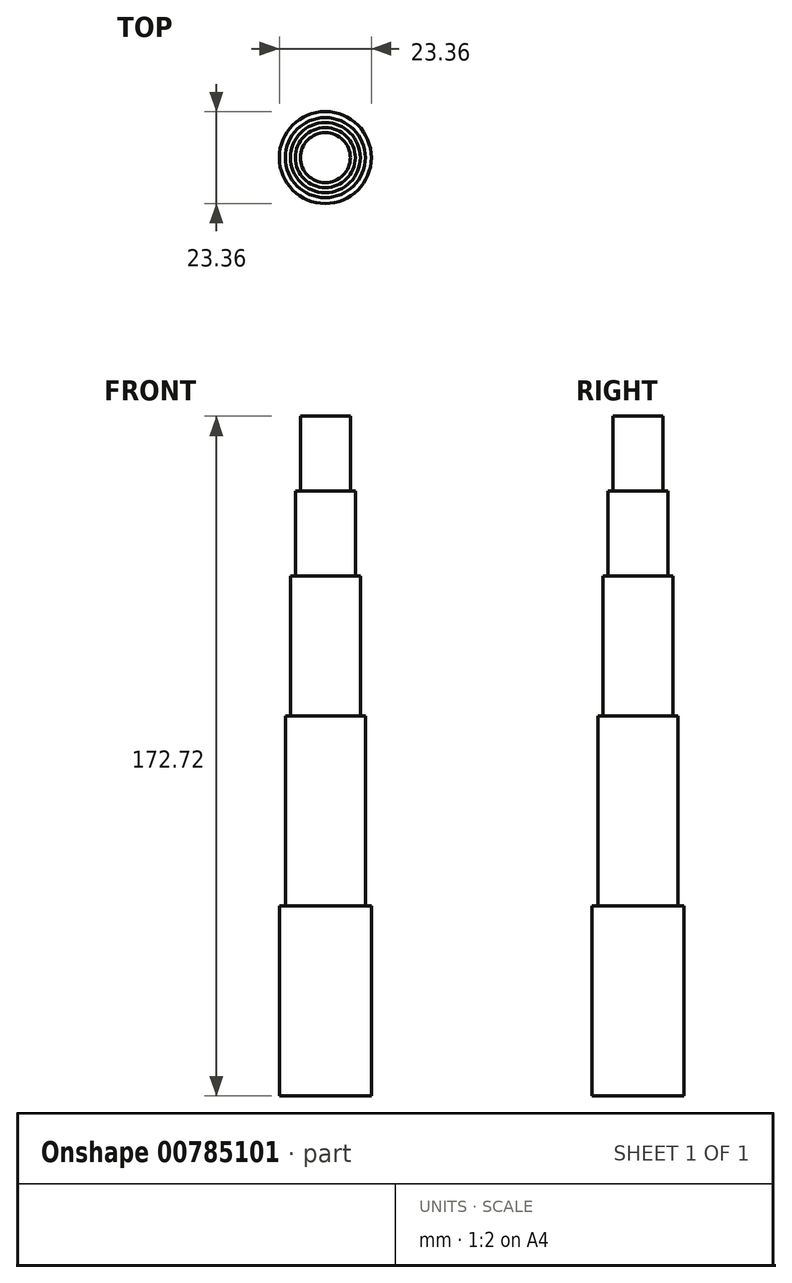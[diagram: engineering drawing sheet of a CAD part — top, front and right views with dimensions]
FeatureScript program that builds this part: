
annotation { "Feature Type Name" : "Feature", "Feature Type Description" : "" }
export const myFeature = defineFeature(function(context is Context, id is Id, definition is map)
    precondition{}
    {
        {
            var Q0;
            Q0=qCreatedBy(makeId("Top.planeOp"),FACE);
            var sketch = newSketch(context, id + "F0", { "sketchPlane" : qUnion([Q0])});
            skCircle(sketch, "E0", {"center": v(0, 0) * mm, "radius": 6.35 * mm});
            skSolve(sketch);
        }
        {
            var Q0;
            Q0 = qSketchRegion(id + "F0", true);
            extrude(context, id + "F1", {"entities" : qUnion([Q0]), "depth" : 19.05 * mm, "offsetDistance" : 25.4 * mm});
        }
        {
            var Q0;
            Q0=qCreatedBy(makeId("Top.planeOp"),FACE);
            var sketch = newSketch(context, id + "F2", { "sketchPlane" : qUnion([Q0])});
            skCircle(sketch, "E1", {"center": v(0, 0) * mm, "radius": 7.62 * mm});
            skSolve(sketch);
        }
        {
            var Q0;
            Q0 = qSketchRegion(id + "F2", true);
            extrude(context, id + "F3", {"entities" : qUnion([Q0]), "operationType" : NewBodyOperationType.ADD, "oppositeDirection" : true, "depth" : 21.59 * mm, "offsetDistance" : 25.4 * mm});
        }
        {
            var Q0;
            Q0=qCreatedBy(makeId("Top.planeOp"),FACE);
            cPlane(context, id + "F4", {"entities" : qUnion([Q0]), "cplaneType" : CPlaneType.OFFSET, "offset" : 21.59 * mm, "oppositeDirection" : true, "width" : 152.4 * mm, "height" : 152.4 * mm});
        }
        {
            var Q0;
            Q0=qCreatedBy(id+"F4.planeOp",FACE);
            var sketch = newSketch(context, id + "F5", { "sketchPlane" : qUnion([Q0])});
            skCircle(sketch, "E2", {"center": v(0, 0) * mm, "radius": 8.9 * mm});
            skSolve(sketch);
        }
        {
            var Q0;
            Q0 = qSketchRegion(id + "F5", true);
            extrude(context, id + "F6", {"entities" : qUnion([Q0]), "operationType" : NewBodyOperationType.ADD, "oppositeDirection" : true, "depth" : 35.56 * mm, "offsetDistance" : 25.4 * mm});
        }
        {
            var Q0;
            Q0=qCreatedBy(id+"F4.planeOp",FACE);
            cPlane(context, id + "F7", {"entities" : qUnion([Q0]), "cplaneType" : CPlaneType.OFFSET, "offset" : 35.56 * mm, "oppositeDirection" : true, "width" : 152.4 * mm, "height" : 152.4 * mm});
        }
        {
            var Q0;
            Q0=qCreatedBy(id+"F7.planeOp",FACE);
            var sketch = newSketch(context, id + "F8", { "sketchPlane" : qUnion([Q0])});
            skCircle(sketch, "E3", {"center": v(0, 0) * mm, "radius": 10.16 * mm});
            skSolve(sketch);
        }
        {
            var Q0;
            Q0 = qSketchRegion(id + "F8", true);
            extrude(context, id + "F9", {"entities" : qUnion([Q0]), "operationType" : NewBodyOperationType.ADD, "oppositeDirection" : true, "depth" : 48.26 * mm, "offsetDistance" : 25.4 * mm});
        }
        {
            var Q0;
            Q0=qCreatedBy(id+"F7.planeOp",FACE);
            cPlane(context, id + "F10", {"entities" : qUnion([Q0]), "cplaneType" : CPlaneType.OFFSET, "offset" : 48.26 * mm, "oppositeDirection" : true, "width" : 152.4 * mm, "height" : 152.4 * mm});
        }
        {
            var Q0;
            Q0=qCreatedBy(id+"F10.planeOp",FACE);
            var sketch = newSketch(context, id + "F11", { "sketchPlane" : qUnion([Q0])});
            skCircle(sketch, "E4", {"center": v(0, 0) * mm, "radius": 11.68 * mm});
            skSolve(sketch);
        }
        {
            var Q0;
            Q0 = qSketchRegion(id + "F11", true);
            extrude(context, id + "F12", {"entities" : qUnion([Q0]), "operationType" : NewBodyOperationType.ADD, "oppositeDirection" : true, "depth" : 48.26 * mm, "offsetDistance" : 25.4 * mm});
        }
    });
